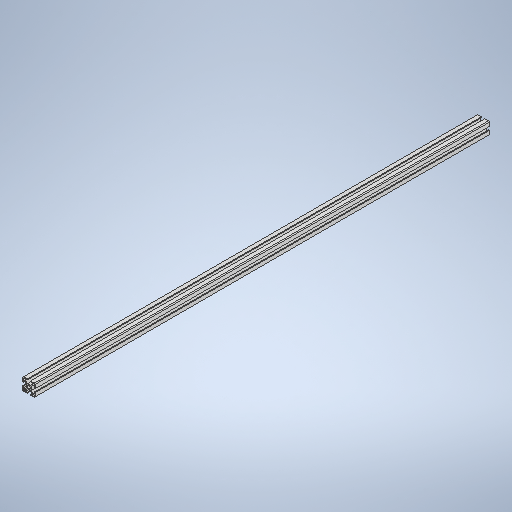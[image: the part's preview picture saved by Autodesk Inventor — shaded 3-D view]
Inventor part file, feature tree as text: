
AUTODESK INVENTOR PART (.ipt)
format: ipt  version: 2025 (Build 290162000, 162)  size: 314,368 bytes
history: native  units: in
note: dims shown in document units (in); Inventor stores cm internally (conversion verified against a paired STEP export)
features: extrude x1, sketch x1
ambient origin geometry x8: Origin, YZ Plane, XZ Plane, XY Plane, X Axis, Y Axis, Z Axis, Center Point
bodies: Solid1 (feature_tree)
feature tree (2):
  extrude  "Extrusion1"  Depth=43.3071in
  sketch  "Sketch1"  dims[d6=43.3071in d7=0.0in d8=0.1969in d9=0.0344in]
